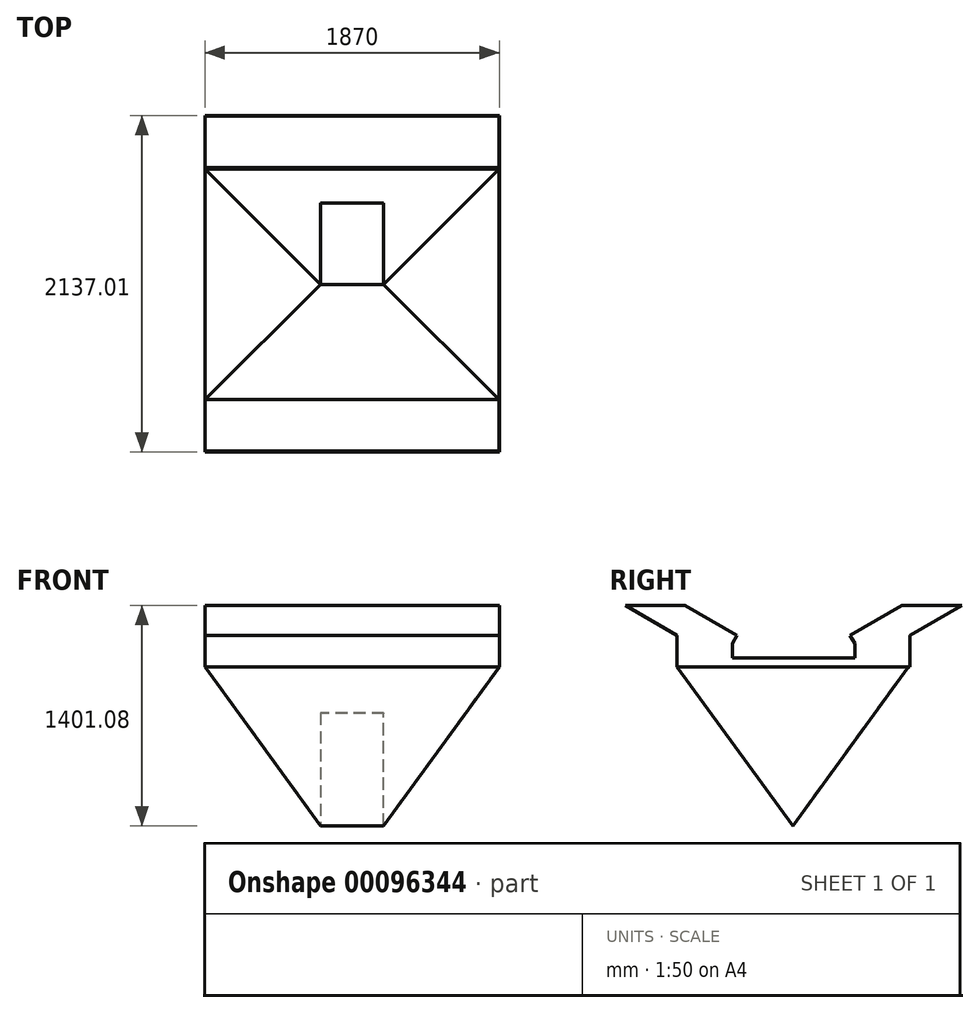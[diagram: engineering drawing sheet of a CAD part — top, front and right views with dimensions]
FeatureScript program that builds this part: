
annotation { "Feature Type Name" : "Feature", "Feature Type Description" : "" }
export const myFeature = defineFeature(function(context is Context, id is Id, definition is map)
    precondition{}
    {
        {
            var Q0;
            Q0=qCreatedBy(makeId("Top.planeOp"),FACE);
            var sketch = newSketch(context, id + "F0", { "sketchPlane" : qUnion([Q0])});
            skLineSegment(sketch, "E0.bottom", {"start": v(0, 0) * mm, "end": v(1870, 0) * mm});
            skLineSegment(sketch, "E0.top", {"start": v(0, 1469.5) * mm, "end": v(1870, 1469.5) * mm});
            skLineSegment(sketch, "E0.left", {"start": v(0, 0) * mm, "end": v(0, 1469.5) * mm});
            skLineSegment(sketch, "E0.right", {"start": v(1870, 0) * mm, "end": v(1870, 1469.5) * mm});
            skSolve(sketch);
        }
        {
            var Q0;
            Q0=makeQuery(id+"F0.imprint","IMPRINT",FACE,{"disambiguationData":[TD([[makeQuery(id+"F0.imprint","IMPRINT",EDGE,{"derivedFrom":sQuery(id+"F0.wireOp",EDGE,"E0.bottom")}),1.0]])]});
            extrude(context, id + "F1", {"entities" : qUnion([Q0]), "oppositeDirection" : true, "depth" : 1011.3 * mm});
        }
        {
            var Q0;
            Q0=makeQuery(id+"F1.opExtrude","SWEPT_FACE",FACE,{"disambiguationData":[OSD([sQuery(id+"F0.wireOp",EDGE,"E0.right")])]});
            var sketch = newSketch(context, id + "F2", { "sketchPlane" : qUnion([Q0])});
            skLineSegment(sketch, "E1", {"start": v(0, 0) * mm, "end": v(734.75, -1011.3) * mm});
            skLineSegment(sketch, "E2", {"start": v(734.75, -1011.3) * mm, "end": v(1469.5, 0) * mm});
            skLineSegment(sketch, "E3", {"start": v(1469.5, 0) * mm, "end": v(0, 0) * mm});
            skSolve(sketch);
        }
        {
            var Q0;
            {var subQ0=sQuery(id+"F2.wireOp",EDGE,"E1");Q0=makeQuery(id+"F2.imprint","IMPRINT",FACE,{"disambiguationData":[TD([[makeQuery(id+"F2.imprint","IMPRINT",EDGE,{"derivedFrom":subQ0}),-1.0]])]});}
            var Q1;
            {var subQ0=sQuery(id+"F2.wireOp",EDGE,"E2");Q1=makeQuery(id+"F2.imprint","IMPRINT",FACE,{"disambiguationData":[TD([[makeQuery(id+"F2.imprint","IMPRINT",EDGE,{"derivedFrom":subQ0}),-1.0]])]});}
            extrude(context, id + "F3", {"entities" : qUnion([Q0, Q1]), "operationType" : NewBodyOperationType.REMOVE, "endBound" : BoundingType.THROUGH_ALL, "oppositeDirection" : true, "depth" : 25 * mm});
        }
        {
            var Q0;
            {var subQ0=sQuery(id+"F0.wireOp",EDGE,"E0.bottom");Q0=makeQuery(id+"F3.boolean.opBoolean","MERGE",EDGE,{"derivedFrom":[makeQuery(id+"F1.opExtrude","CAP_EDGE",EDGE,{"disambiguationData":[OSD([subQ0])],"isStart":true}),makeQuery(id+"F3.opExtrude","SWEPT_EDGE",EDGE,{"disambiguationData":[OSD([subQ0,sQuery(id+"F0.wireOp",EDGE,"E0.right"),sQuery(id+"F2.wireOp",EDGE,"E1"),sQuery(id+"F2.wireOp",EDGE,"E3")])]})]});}
            cPlane(context, id + "F4", {"entities" : qUnion([Q0]), "cplaneType" : CPlaneType.LINE_ANGLE, "offset" : 150 * mm, "angle" : 0 * degree, "width" : 150 * mm, "height" : 150 * mm});
        }
        {
            var Q0;
            Q0=qCreatedBy(id+"F4.planeOp",FACE);
            var sketch = newSketch(context, id + "F5", { "sketchPlane" : qUnion([Q0])});
            skLineSegment(sketch, "E4", {"start": v(0, 0) * mm, "end": v(-1870, 0) * mm});
            skLineSegment(sketch, "E5", {"start": v(-1870, 0) * mm, "end": v(-1135, -1011.08) * mm});
            skLineSegment(sketch, "E6", {"start": v(-1135, -1011.08) * mm, "end": v(-735, -1011.08) * mm});
            skLineSegment(sketch, "E7", {"start": v(-735, -1011.08) * mm, "end": v(0, 0) * mm});
            skLineSegment(sketch, "E8", {"start": v(0, 0) * mm, "end": v(0, -1011.08) * mm});
            skLineSegment(sketch, "E9", {"start": v(-735, -1011.08) * mm, "end": v(-1135, -1011.08) * mm});
            skLineSegment(sketch, "E10", {"start": v(0, 0) * mm, "end": v(0, -1118.93) * mm});
            skLineSegment(sketch, "E11", {"start": v(0, -1118.93) * mm, "end": v(-1870, -1118.93) * mm});
            skLineSegment(sketch, "E12", {"start": v(-1870, -1118.93) * mm, "end": v(-1870, 0) * mm});
            skSolve(sketch);
        }
        {
            var Q0;
            Q0=makeQuery(id+"F5.imprint","IMPRINT",FACE,{"disambiguationData":[TD([[makeQuery(id+"F5.imprint","IMPRINT",EDGE,{"derivedFrom":sQuery(id+"F5.wireOp",EDGE,"E5")}),-1.0]])]});
            extrude(context, id + "F6", {"entities" : qUnion([Q0]), "operationType" : NewBodyOperationType.REMOVE, "endBound" : BoundingType.THROUGH_ALL, "depth" : 25 * mm});
        }
        {
            var Q0;
            Q0=qCreatedBy(makeId("Right.planeOp"),FACE);
            var sketch = newSketch(context, id + "F7", { "sketchPlane" : qUnion([Q0])});
            skLineSegment(sketch, "E13", {"start": v(0, 0) * mm, "end": v(1478.83, 0) * mm});
            skLineSegment(sketch, "E14", {"start": v(1478.83, 0) * mm, "end": v(1478.83, 200) * mm});
            skLineSegment(sketch, "E15", {"start": v(0, 0) * mm, "end": v(0, 200) * mm});
            skLineSegment(sketch, "E16", {"start": v(0, 200) * mm, "end": v(-329.09, 390) * mm});
            skLineSegment(sketch, "E17", {"start": v(-329.09, 390) * mm, "end": v(50.91, 390) * mm});
            skLineSegment(sketch, "E18", {"start": v(50.91, 390) * mm, "end": v(380, 200) * mm});
            skLineSegment(sketch, "E19", {"start": v(739.41, 0) * mm, "end": v(739.41, 58.04) * mm});
            skLineSegment(sketch, "E20.MirrorCS", {"start": v(1478.83, 200) * mm, "end": v(1807.92, 390) * mm});
            skLineSegment(sketch, "E21.MirrorCS", {"start": v(1807.92, 390) * mm, "end": v(1427.92, 390) * mm});
            skLineSegment(sketch, "E22.MirrorCS", {"start": v(1427.92, 390) * mm, "end": v(1098.83, 200) * mm});
            skLineSegment(sketch, "E23", {"start": v(380, 200) * mm, "end": v(350, 148.04) * mm});
            skLineSegment(sketch, "E24", {"start": v(350, 148.04) * mm, "end": v(350, 58.04) * mm});
            skLineSegment(sketch, "E25", {"start": v(350, 58.04) * mm, "end": v(739.41, 58.04) * mm});
            skLineSegment(sketch, "E26.MirrorCS", {"start": v(1098.83, 200) * mm, "end": v(1128.83, 148.04) * mm});
            skLineSegment(sketch, "E27.MirrorCS", {"start": v(1128.83, 58.04) * mm, "end": v(739.41, 58.04) * mm});
            skLineSegment(sketch, "E28.MirrorCS", {"start": v(1128.83, 148.04) * mm, "end": v(1128.83, 58.04) * mm});
            skSolve(sketch);
        }
        {
            var Q0;
            Q0 = qSketchRegion(id + "F7", true);
            extrude(context, id + "F8", {"entities" : qUnion([Q0]), "operationType" : NewBodyOperationType.ADD, "depth" : 1870 * mm});
        }
        {
            var Q0;
            Q0=makeQuery(id+"F8.opExtrude","SWEPT_FACE",FACE,{"disambiguationData":[OSD([sQuery(id+"F7.wireOp",EDGE,"E25"),sQuery(id+"F7.wireOp",EDGE,"E27.MirrorCS")])]});
            var Q1;
            Q1=makeQuery(id+"F8.opExtrude","SWEPT_FACE",FACE,{"disambiguationData":[OSD([sQuery(id+"F7.wireOp",EDGE,"E17")])]});
            var Q2;
            Q2=makeQuery(id+"F8.opExtrude","SWEPT_FACE",FACE,{"disambiguationData":[OSD([sQuery(id+"F7.wireOp",EDGE,"E18")])]});
            var Q3;
            Q3=makeQuery(id+"F8.opExtrude","SWEPT_FACE",FACE,{"disambiguationData":[OSD([sQuery(id+"F7.wireOp",EDGE,"E24")])]});
            var Q4;
            Q4=makeQuery(id+"F8.opExtrude","SWEPT_FACE",FACE,{"disambiguationData":[OSD([sQuery(id+"F7.wireOp",EDGE,"E23")])]});
            var Q5;
            Q5=makeQuery(id+"F8.opExtrude","SWEPT_FACE",FACE,{"disambiguationData":[OSD([sQuery(id+"F7.wireOp",EDGE,"E28.MirrorCS")])]});
            var Q6;
            Q6=makeQuery(id+"F8.opExtrude","SWEPT_FACE",FACE,{"disambiguationData":[OSD([sQuery(id+"F7.wireOp",EDGE,"E26.MirrorCS")])]});
            var Q7;
            Q7=makeQuery(id+"F8.opExtrude","SWEPT_FACE",FACE,{"disambiguationData":[OSD([sQuery(id+"F7.wireOp",EDGE,"E22.MirrorCS")])]});
            var Q8;
            Q8=makeQuery(id+"F8.opExtrude","SWEPT_FACE",FACE,{"disambiguationData":[OSD([sQuery(id+"F7.wireOp",EDGE,"E21.MirrorCS")])]});
            shell(context, id + "F9", {"entities" : qUnion([Q0, Q1, Q2, Q3, Q4, Q5, Q6, Q7, Q8]), "thickness" : 2.5 * mm});
        }
        {
            var Q0;
            Q0=makeQuery(id+"F3.boolean.opBoolean","COPY",FACE,{"derivedFrom":makeQuery(id+"F3.opExtrude","SWEPT_FACE",FACE,{"disambiguationData":[OSD([sQuery(id+"F2.wireOp",EDGE,"E2")])]})});
            var sketch = newSketch(context, id + "F10", { "sketchPlane" : qUnion([Q0])});
            skLineSegment(sketch, "E29", {"start": v(-1135, -386) * mm, "end": v(-1135, 498.48) * mm});
            skLineSegment(sketch, "E30", {"start": v(-1135, 498.48) * mm, "end": v(-735, 498.48) * mm});
            skLineSegment(sketch, "E31", {"start": v(-735, 498.48) * mm, "end": v(-735, -386) * mm});
            skSolve(sketch);
        }
        {
            var Q0;
            Q0 = qSketchRegion(id + "F10", true);
            var Q1;
            Q1=makeQuery(id+"F10.imprint","IMPRINT",FACE,{"disambiguationData":[TD([[makeQuery(id+"F10.imprint","IMPRINT",EDGE,{"derivedFrom":sQuery(id+"F10.wireOp",EDGE,"E29")}),-1.0]])]});
            extrude(context, id + "F11", {"entities" : qUnion([Q0, Q1]), "operationType" : NewBodyOperationType.REMOVE, "oppositeDirection" : true, "depth" : 2.5 * mm});
        }
    });
